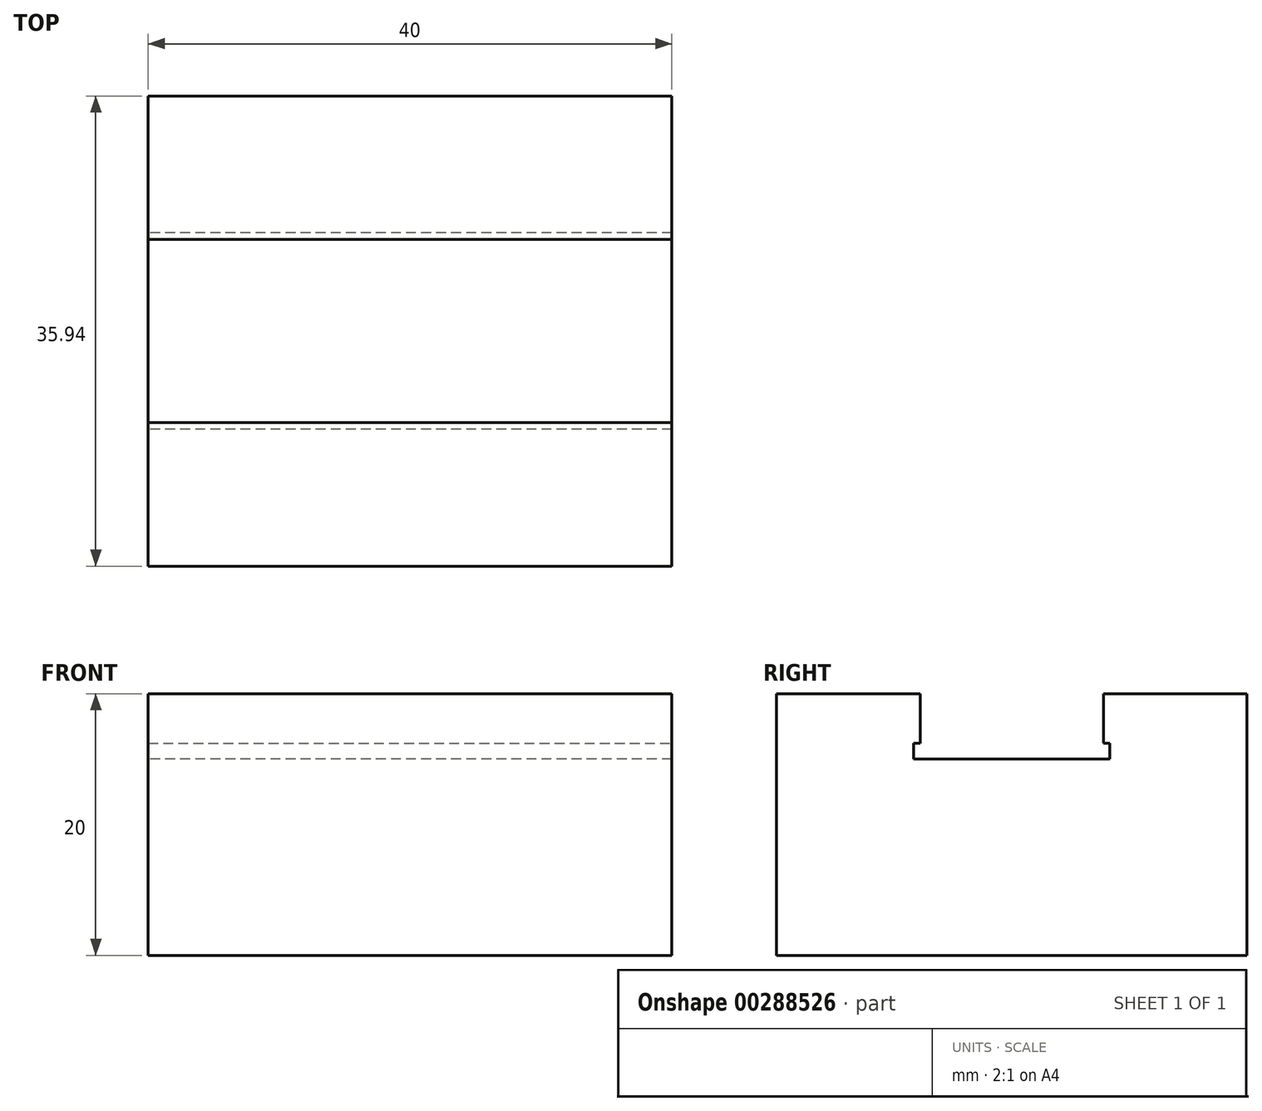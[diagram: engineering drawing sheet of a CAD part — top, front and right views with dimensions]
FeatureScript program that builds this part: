
annotation { "Feature Type Name" : "Feature", "Feature Type Description" : "" }
export const myFeature = defineFeature(function(context is Context, id is Id, definition is map)
    precondition{}
    {
        {
            var Q0;
            Q0=qCreatedBy(makeId("Top.planeOp"),FACE);
            var sketch = newSketch(context, id + "F0", { "sketchPlane" : qUnion([Q0])});
            skLineSegment(sketch, "E0.bottom", {"start": v(-20, 17.97) * mm, "end": v(20, 17.97) * mm});
            skLineSegment(sketch, "E0.top", {"start": v(-20, -17.97) * mm, "end": v(20, -17.97) * mm});
            skLineSegment(sketch, "E0.left", {"start": v(-20, 17.97) * mm, "end": v(-20, -17.97) * mm});
            skLineSegment(sketch, "E0.right", {"start": v(20, 17.97) * mm, "end": v(20, -17.97) * mm});
            skPoint(sketch, "E0.middle", {"position": v(0, 0) * mm});
            skSolve(sketch);
        }
        {
            var Q0;
            Q0=makeQuery(id+"F0.imprint","IMPRINT",FACE,{"disambiguationData":[TD([[makeQuery(id+"F0.imprint","IMPRINT",EDGE,{"derivedFrom":sQuery(id+"F0.wireOp",EDGE,"E0.bottom")}),-1.0]])]});
            extrude(context, id + "F1", {"entities" : qUnion([Q0]), "depth" : 20 * mm});
        }
        {
            var Q0;
            Q0=makeQuery(id+"F1.opExtrude","CAP_FACE",FACE,{"disambiguationData":[OSD([sQuery(id+"F0.wireOp",EDGE,"E0.bottom"),sQuery(id+"F0.wireOp",EDGE,"E0.top"),sQuery(id+"F0.wireOp",EDGE,"E0.left"),sQuery(id+"F0.wireOp",EDGE,"E0.right")])],"isStart":false});
            var sketch = newSketch(context, id + "F2", { "sketchPlane" : qUnion([Q0])});
            skLineSegment(sketch, "E1.bottom", {"start": v(20, 7) * mm, "end": v(-8, 7) * mm});
            skLineSegment(sketch, "E1.top", {"start": v(20, -7) * mm, "end": v(-8, -7) * mm});
            skLineSegment(sketch, "E1.left", {"start": v(20, 7) * mm, "end": v(20, -7) * mm});
            skLineSegment(sketch, "E1.right", {"start": v(-8, 7) * mm, "end": v(-8, -7) * mm});
            skSolve(sketch);
        }
        {
            var Q0;
            Q0 = qSketchRegion(id + "F2", true);
            extrude(context, id + "F3", {"entities" : qUnion([Q0]), "operationType" : NewBodyOperationType.REMOVE, "oppositeDirection" : true, "depth" : 5 * mm});
        }
        {
            var Q0;
            Q0=makeQuery(id+"F3.boolean.opBoolean","COPY",FACE,{"derivedFrom":makeQuery(id+"F3.opExtrude","SWEPT_FACE",FACE,{"disambiguationData":[OSD([sQuery(id+"F2.wireOp",EDGE,"E1.right")])]})});
            var sketch = newSketch(context, id + "F4", { "sketchPlane" : qUnion([Q0])});
            skLineSegment(sketch, "E2.bottom", {"start": v(7, 15) * mm, "end": v(-7, 15) * mm});
            skLineSegment(sketch, "E2.top", {"start": v(7, 16.12) * mm, "end": v(-7, 16.12) * mm});
            skLineSegment(sketch, "E2.left", {"start": v(7, 15) * mm, "end": v(7, 16.12) * mm});
            skLineSegment(sketch, "E2.right", {"start": v(-7, 15) * mm, "end": v(-7, 16.12) * mm});
            skSolve(sketch);
        }
        {
            var Q0;
            Q0=makeQuery(id+"F4.imprint","IMPRINT",FACE,{"disambiguationData":[TD([[makeQuery(id+"F4.imprint","IMPRINT",EDGE,{"derivedFrom":sQuery(id+"F4.wireOp",EDGE,"E2.bottom")}),-1.0]])]});
            extrude(context, id + "F5", {"entities" : qUnion([Q0]), "operationType" : NewBodyOperationType.REMOVE, "oppositeDirection" : true, "depth" : 3 * mm});
        }
        {
            var Q0;
            Q0=makeQuery(id+"F5.boolean.opBoolean","COPY",FACE,{"derivedFrom":makeQuery(id+"F5.opExtrude","SWEPT_FACE",FACE,{"disambiguationData":[OSD([sQuery(id+"F4.wireOp",EDGE,"E2.top")])]})});
            var sketch = newSketch(context, id + "F6", { "sketchPlane" : qUnion([Q0])});
            skLineSegment(sketch, "E3.bottom", {"start": v(-8, -4) * mm, "end": v(-11, -4) * mm});
            skLineSegment(sketch, "E3.top", {"start": v(-8, -3) * mm, "end": v(-11, -3) * mm});
            skLineSegment(sketch, "E3.left", {"start": v(-8, -4) * mm, "end": v(-8, -3) * mm});
            skLineSegment(sketch, "E3.right", {"start": v(-11, -4) * mm, "end": v(-11, -3) * mm});
            skLineSegment(sketch, "E4.bottom", {"start": v(-8, -2.75) * mm, "end": v(-11, -2.75) * mm});
            skLineSegment(sketch, "E4.top", {"start": v(-8, -1.75) * mm, "end": v(-11, -1.75) * mm});
            skLineSegment(sketch, "E4.left", {"start": v(-8, -2.75) * mm, "end": v(-8, -1.75) * mm});
            skLineSegment(sketch, "E4.right", {"start": v(-11, -2.75) * mm, "end": v(-11, -1.75) * mm});
            skLineSegment(sketch, "E5.bottom", {"start": v(-8, -1.5) * mm, "end": v(-11, -1.5) * mm});
            skLineSegment(sketch, "E5.top", {"start": v(-8, -0.5) * mm, "end": v(-11, -0.5) * mm});
            skLineSegment(sketch, "E5.left", {"start": v(-8, -1.5) * mm, "end": v(-8, -0.5) * mm});
            skLineSegment(sketch, "E5.right", {"start": v(-11, -1.5) * mm, "end": v(-11, -0.5) * mm});
            skLineSegment(sketch, "E6.bottom", {"start": v(-8, -0.25) * mm, "end": v(-11, -0.25) * mm});
            skLineSegment(sketch, "E6.top", {"start": v(-8, 0.75) * mm, "end": v(-11, 0.75) * mm});
            skLineSegment(sketch, "E6.left", {"start": v(-8, -0.25) * mm, "end": v(-8, 0.75) * mm});
            skLineSegment(sketch, "E6.right", {"start": v(-11, -0.25) * mm, "end": v(-11, 0.75) * mm});
            skPoint(sketch, "E7", {"position": v(-11, -3.5) * mm});
            skPoint(sketch, "E8", {"position": v(-11, -2.25) * mm});
            skPoint(sketch, "E9", {"position": v(-11, -1) * mm});
            skPoint(sketch, "E10", {"position": v(-11, 0.25) * mm});
            skSolve(sketch);
        }
        {
            var Q0;
            Q0 = qSketchRegion(id + "F6", true);
            extrude(context, id + "F7", {"entities" : qUnion([Q0]), "operationType" : NewBodyOperationType.REMOVE, "oppositeDirection" : true, "depth" : 0.5 * mm});
        }
        {
            var Q0;
            Q0=makeQuery(id+"F1.opExtrude","CAP_FACE",FACE,{"disambiguationData":[OSD([sQuery(id+"F0.wireOp",EDGE,"E0.bottom"),sQuery(id+"F0.wireOp",EDGE,"E0.top"),sQuery(id+"F0.wireOp",EDGE,"E0.left"),sQuery(id+"F0.wireOp",EDGE,"E0.right")])],"isStart":false});
            var sketch = newSketch(context, id + "F8", { "sketchPlane" : qUnion([Q0])});
            skLineSegment(sketch, "E11.bottom", {"start": v(-8, -7) * mm, "end": v(-20, -7) * mm});
            skLineSegment(sketch, "E11.top", {"start": v(-8, 7) * mm, "end": v(-20, 7) * mm});
            skLineSegment(sketch, "E11.left", {"start": v(-8, -7) * mm, "end": v(-8, 7) * mm});
            skLineSegment(sketch, "E11.right", {"start": v(-20, -7) * mm, "end": v(-20, 7) * mm});
            skSolve(sketch);
        }
        {
            var Q0;
            Q0 = qSketchRegion(id + "F8", true);
            extrude(context, id + "F9", {"entities" : qUnion([Q0]), "operationType" : NewBodyOperationType.REMOVE, "oppositeDirection" : true, "depth" : 2.5 * mm});
        }
        {
            var Q0;
            Q0=makeQuery(id+"F7.boolean.opBoolean","MERGE",FACE,{"derivedFrom":[makeQuery(id+"F5.boolean.opBoolean","COPY",FACE,{"derivedFrom":makeQuery(id+"F5.opExtrude","CAP_FACE",FACE,{"disambiguationData":[OSD([sQuery(id+"F4.wireOp",EDGE,"E2.bottom"),sQuery(id+"F4.wireOp",EDGE,"E2.top"),sQuery(id+"F4.wireOp",EDGE,"E2.left"),sQuery(id+"F4.wireOp",EDGE,"E2.right")])],"isStart":false})}),makeQuery(id+"F7.opExtrude","SWEPT_FACE",FACE,{"disambiguationData":[OSD([sQuery(id+"F6.wireOp",EDGE,"E3.right")])]}),makeQuery(id+"F7.opExtrude","SWEPT_FACE",FACE,{"disambiguationData":[OSD([sQuery(id+"F6.wireOp",EDGE,"E4.right")])]}),makeQuery(id+"F7.opExtrude","SWEPT_FACE",FACE,{"disambiguationData":[OSD([sQuery(id+"F6.wireOp",EDGE,"E5.right")])]}),makeQuery(id+"F7.opExtrude","SWEPT_FACE",FACE,{"disambiguationData":[OSD([sQuery(id+"F6.wireOp",EDGE,"E6.right")])]})]});
            extrude(context, id + "F10", {"entities" : qUnion([Q0]), "operationType" : NewBodyOperationType.REMOVE, "oppositeDirection" : true, "depth" : 25 * mm});
        }
        {
            var Q0;
            Q0=makeQuery(id+"F9.boolean.opBoolean","COPY",FACE,{"derivedFrom":makeQuery(id+"F9.opExtrude","CAP_FACE",FACE,{"disambiguationData":[OSD([sQuery(id+"F8.wireOp",EDGE,"E11.bottom"),sQuery(id+"F8.wireOp",EDGE,"E11.top"),sQuery(id+"F8.wireOp",EDGE,"E11.left"),sQuery(id+"F8.wireOp",EDGE,"E11.right")])],"isStart":false})});
            var sketch = newSketch(context, id + "F11", { "sketchPlane" : qUnion([Q0])});
            skLineSegment(sketch, "E12.bottom", {"start": v(-8, 7) * mm, "end": v(-17.05, 7) * mm});
            skLineSegment(sketch, "E12.top", {"start": v(-8, 5.73) * mm, "end": v(-17.05, 5.73) * mm});
            skLineSegment(sketch, "E12.left", {"start": v(-8, 7) * mm, "end": v(-8, 5.73) * mm});
            skLineSegment(sketch, "E12.right", {"start": v(-17.05, 7) * mm, "end": v(-17.05, 5.73) * mm});
            skLineSegment(sketch, "E13.bottom", {"start": v(-8, -7) * mm, "end": v(-17.05, -7) * mm});
            skLineSegment(sketch, "E13.top", {"start": v(-8, -1.77) * mm, "end": v(-17.05, -1.77) * mm});
            skLineSegment(sketch, "E13.left", {"start": v(-8, -7) * mm, "end": v(-8, -1.77) * mm});
            skLineSegment(sketch, "E13.right", {"start": v(-17.05, -7) * mm, "end": v(-17.05, -1.77) * mm});
            skSolve(sketch);
        }
        {
            var Q0;
            Q0 = qSketchRegion(id + "F11", true);
            var Q1;
            {var subQ0=sQuery(id+"F4.wireOp",EDGE,"E2.bottom");Q1=makeQuery(id+"F10.boolean.opBoolean","MERGE",FACE,{"derivedFrom":[makeQuery(id+"F5.boolean.opBoolean","MERGE",FACE,{"derivedFrom":[makeQuery(id+"F3.boolean.opBoolean","COPY",FACE,{"derivedFrom":makeQuery(id+"F3.opExtrude","CAP_FACE",FACE,{"disambiguationData":[OSD([sQuery(id+"F2.wireOp",EDGE,"E1.bottom"),sQuery(id+"F2.wireOp",EDGE,"E1.top"),sQuery(id+"F2.wireOp",EDGE,"E1.left"),sQuery(id+"F2.wireOp",EDGE,"E1.right")])],"isStart":false})}),makeQuery(id+"F5.opExtrude","SWEPT_FACE",FACE,{"disambiguationData":[OSD([subQ0])]})]}),makeQuery(id+"F10.opExtrude","SWEPT_FACE",FACE,{"disambiguationData":[OSD([subQ0])]})]});}
            extrude(context, id + "F12", {"entities" : qUnion([Q0]), "operationType" : NewBodyOperationType.REMOVE, "endBound" : BoundingType.UP_TO_SURFACE, "oppositeDirection" : true, "endBoundEntityFace" : qUnion([Q1]), "depth" : 25 * mm});
        }
        {
            var Q0;
            {var subQ0=sQuery(id+"F4.wireOp",EDGE,"E2.right");Q0=makeQuery(id+"F12.boolean.opBoolean","MERGE",FACE,{"derivedFrom":[makeQuery(id+"F10.boolean.opBoolean","MERGE",FACE,{"derivedFrom":[makeQuery(id+"F9.boolean.opBoolean","MERGE",FACE,{"derivedFrom":[makeQuery(id+"F5.boolean.opBoolean","MERGE",FACE,{"derivedFrom":[makeQuery(id+"F3.boolean.opBoolean","COPY",FACE,{"derivedFrom":makeQuery(id+"F3.opExtrude","SWEPT_FACE",FACE,{"disambiguationData":[OSD([sQuery(id+"F2.wireOp",EDGE,"E1.top")])]})}),makeQuery(id+"F5.opExtrude","SWEPT_FACE",FACE,{"disambiguationData":[OSD([subQ0])]})]}),makeQuery(id+"F9.opExtrude","SWEPT_FACE",FACE,{"disambiguationData":[OSD([sQuery(id+"F8.wireOp",EDGE,"E11.bottom")])]})]}),makeQuery(id+"F10.opExtrude","SWEPT_FACE",FACE,{"disambiguationData":[OSD([subQ0])]})]}),makeQuery(id+"F12.opExtrude","SWEPT_FACE",FACE,{"disambiguationData":[OSD([sQuery(id+"F11.wireOp",EDGE,"E13.bottom")])]})]});}
            var sketch = newSketch(context, id + "F13", { "sketchPlane" : qUnion([Q0])});
            skLineSegment(sketch, "E14.bottom", {"start": v(20, 15) * mm, "end": v(-20, 15) * mm});
            skLineSegment(sketch, "E14.top", {"start": v(20, 16.2) * mm, "end": v(-20, 16.2) * mm});
            skLineSegment(sketch, "E14.left", {"start": v(20, 15) * mm, "end": v(20, 16.2) * mm});
            skLineSegment(sketch, "E14.right", {"start": v(-20, 15) * mm, "end": v(-20, 16.2) * mm});
            skSolve(sketch);
        }
        {
            var Q0;
            Q0 = qSketchRegion(id + "F13", true);
            extrude(context, id + "F14", {"entities" : qUnion([Q0]), "operationType" : NewBodyOperationType.REMOVE, "oppositeDirection" : true, "depth" : 0.5 * mm});
        }
        {
            var Q0;
            {var subQ0=sQuery(id+"F4.wireOp",EDGE,"E2.left");Q0=makeQuery(id+"F12.boolean.opBoolean","MERGE",FACE,{"derivedFrom":[makeQuery(id+"F10.boolean.opBoolean","MERGE",FACE,{"derivedFrom":[makeQuery(id+"F9.boolean.opBoolean","MERGE",FACE,{"derivedFrom":[makeQuery(id+"F5.boolean.opBoolean","MERGE",FACE,{"derivedFrom":[makeQuery(id+"F3.boolean.opBoolean","COPY",FACE,{"derivedFrom":makeQuery(id+"F3.opExtrude","SWEPT_FACE",FACE,{"disambiguationData":[OSD([sQuery(id+"F2.wireOp",EDGE,"E1.bottom")])]})}),makeQuery(id+"F5.opExtrude","SWEPT_FACE",FACE,{"disambiguationData":[OSD([subQ0])]})]}),makeQuery(id+"F9.opExtrude","SWEPT_FACE",FACE,{"disambiguationData":[OSD([sQuery(id+"F8.wireOp",EDGE,"E11.top")])]})]}),makeQuery(id+"F10.opExtrude","SWEPT_FACE",FACE,{"disambiguationData":[OSD([subQ0])]})]}),makeQuery(id+"F12.opExtrude","SWEPT_FACE",FACE,{"disambiguationData":[OSD([sQuery(id+"F11.wireOp",EDGE,"E12.bottom")])]})]});}
            var sketch = newSketch(context, id + "F15", { "sketchPlane" : qUnion([Q0])});
            skLineSegment(sketch, "E15.bottom", {"start": v(-20, 15) * mm, "end": v(20, 15) * mm});
            skLineSegment(sketch, "E15.top", {"start": v(-20, 16.2) * mm, "end": v(20, 16.2) * mm});
            skLineSegment(sketch, "E15.left", {"start": v(-20, 15) * mm, "end": v(-20, 16.2) * mm});
            skLineSegment(sketch, "E15.right", {"start": v(20, 15) * mm, "end": v(20, 16.2) * mm});
            skSolve(sketch);
        }
        {
            var Q0;
            Q0 = qSketchRegion(id + "F15", true);
            extrude(context, id + "F16", {"entities" : qUnion([Q0]), "operationType" : NewBodyOperationType.REMOVE, "oppositeDirection" : true, "depth" : 0.5 * mm});
        }
        {
            var Q0;
            Q0=makeQuery(id+"F9.boolean.opBoolean","COPY",FACE,{"derivedFrom":makeQuery(id+"F9.opExtrude","CAP_FACE",FACE,{"disambiguationData":[OSD([sQuery(id+"F8.wireOp",EDGE,"E11.bottom"),sQuery(id+"F8.wireOp",EDGE,"E11.top"),sQuery(id+"F8.wireOp",EDGE,"E11.left"),sQuery(id+"F8.wireOp",EDGE,"E11.right")])],"isStart":false})});
            var Q1;
            {var subQ0=sQuery(id+"F4.wireOp",EDGE,"E2.bottom");Q1=makeQuery(id+"F16.boolean.opBoolean","MERGE",FACE,{"derivedFrom":[makeQuery(id+"F14.boolean.opBoolean","MERGE",FACE,{"derivedFrom":[makeQuery(id+"F10.boolean.opBoolean","MERGE",FACE,{"derivedFrom":[makeQuery(id+"F5.boolean.opBoolean","MERGE",FACE,{"derivedFrom":[makeQuery(id+"F3.boolean.opBoolean","COPY",FACE,{"derivedFrom":makeQuery(id+"F3.opExtrude","CAP_FACE",FACE,{"disambiguationData":[OSD([sQuery(id+"F2.wireOp",EDGE,"E1.bottom"),sQuery(id+"F2.wireOp",EDGE,"E1.top"),sQuery(id+"F2.wireOp",EDGE,"E1.left"),sQuery(id+"F2.wireOp",EDGE,"E1.right")])],"isStart":false})}),makeQuery(id+"F5.opExtrude","SWEPT_FACE",FACE,{"disambiguationData":[OSD([subQ0])]})]}),makeQuery(id+"F10.opExtrude","SWEPT_FACE",FACE,{"disambiguationData":[OSD([subQ0])]})]}),makeQuery(id+"F14.opExtrude","SWEPT_FACE",FACE,{"disambiguationData":[OSD([sQuery(id+"F13.wireOp",EDGE,"E14.bottom")])]})]}),makeQuery(id+"F16.opExtrude","SWEPT_FACE",FACE,{"disambiguationData":[OSD([sQuery(id+"F15.wireOp",EDGE,"E15.bottom")])]})]});}
            extrude(context, id + "F17", {"entities" : qUnion([Q0]), "operationType" : NewBodyOperationType.REMOVE, "endBound" : BoundingType.UP_TO_SURFACE, "oppositeDirection" : true, "endBoundEntityFace" : qUnion([Q1]), "depth" : 25 * mm});
        }
    });
